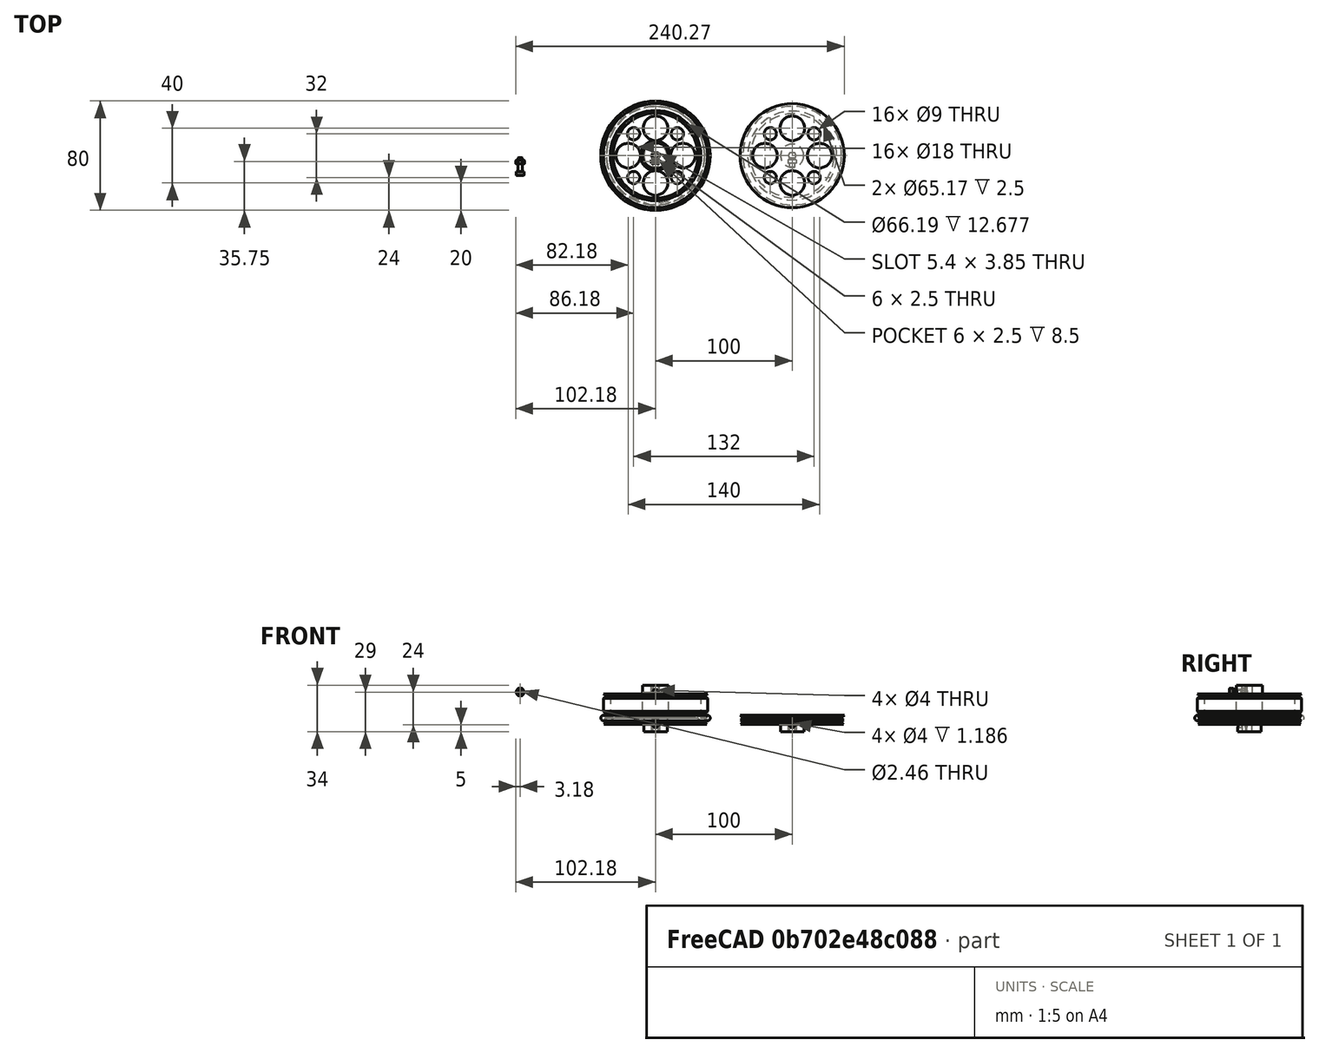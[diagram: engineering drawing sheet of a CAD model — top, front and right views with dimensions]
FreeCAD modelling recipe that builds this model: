
FCSTD DOCUMENT  (FreeCAD 0.19R24291 (Git))
Label: ruedas
License: All rights reserved
LicenseURL: http://en.wikipedia.org/wiki/All_rights_reserved
objects: Part::Cut×11, Part::Cylinder×10, Sketcher::SketchObject×8, PartDesign::Body×6, Part::Feature×6, Part::FeaturePython×6, Part::MultiFuse×5, App::Part×4, Part::Box×3, Part::Extrusion×3, Part::Revolution×2, PartDesign::Revolution×2, Mesh::Feature×2, PartDesign::FeatureBase×1, PartDesign::Pocket×1, PartDesign::PolarPattern×1, Part::Chamfer×1
note: 69 computed .brp shape members not serialized (recipe doc carries the construction recipe); baked Part::Feature solids carry a one-line shape summary decoded from their .brp

FEATURE [PartDesign::Body] Body
  Origin = -> Origin
FEATURE [Sketcher::SketchObject] Sketch
  FullyConstrained = true
  MapMode = 5
  Placement = pos=(0,0,0) rot=(1,0,0;1.5708rad)
  Support = -> [XZ_Plane]
  sketch-geometry (8):
    g0: LineSegment StartX=0 StartY=2 StartZ=0 EndX=31 EndY=2 EndZ=0
    g1: LineSegment StartX=31 StartY=2 StartZ=0 EndX=33 EndY=4 EndZ=0
    g2: LineSegment StartX=33 StartY=4 StartZ=0 EndX=38 EndY=4 EndZ=0
    g3: LineSegment StartX=38 StartY=0 StartZ=0 EndX=0 EndY=0 EndZ=0
    g4: LineSegment StartX=0 StartY=0 StartZ=0 EndX=0 EndY=2 EndZ=0
    g5: Circle CenterX=37.5 CenterY=2 CenterZ=0 NormalX=0 NormalY=0 NormalZ=1 AngleXU=0 Radius=1
    g6: LineSegment StartX=38 StartY=4 StartZ=0 EndX=36.1315 EndY=2 EndZ=0
    g7: LineSegment StartX=36.1315 StartY=2 StartZ=0 EndX=38 EndY=0 EndZ=0
  constraints (24):
    c: PointOnObject(g0,g-2)
    c: Horizontal(g0)
    c: Coincident(g0,g1)
    c: Coincident(g1,g2)
    c: Horizontal(g2)
    c: Horizontal(g3)
    c: Coincident(g3,g4)
    c: Coincident(g4,g0)
    c: Radius(g5) = 1
    c: DistanceX(g-1,g5) = 37.5
    c: Vertical(g4)
    c: DistanceY(g4,g4) = 2
    c: DistanceY(g3,g1) = 4
    c: PointOnObject(g3,g-1)
    c: DistanceY(g3,g5) = 2
    c: Angle(g1,g0) = 2.35619
    c: Coincident(g2,g6)
    c: Coincident(g6,g7)
    c: Coincident(g7,g3)
    c: DistanceY(g3,g6) = 2
    c: Tangent(g7,g5)
    c: Tangent(g6,g5)
    c: DistanceX(g2,g2) = 5
    c: DistanceX(g3,g3) = 38
FEATURE [Part::Box] Box  label="Cubo"
  AttacherType = Attacher::AttachEngine3D
  Height = 10
  Length = 6
  Placement = pos=(-3,3,2.5) rot=(0,0,1;0rad)
  Width = 2.5
FEATURE [Part::Cylinder] Cylinder002  label="Cilindro002"
  Angle = 360
  AttacherType = Attacher::AttachEngine3D
  Height = 10
  Placement = pos=(0,10.2,6) rot=(1,0,0;1.5708rad)
  Radius = 2
FEATURE [Part::Cylinder] Cylinder  label="Cilindro"
  Angle = 360
  AttacherType = Attacher::AttachEngine3D
  Height = 11
  Radius = 8.5
FEATURE [Part::Cut] Cut
  Base = -> Cylinder
  Tool = -> Box
FEATURE [Part::Cut] Cut002
  Base = -> Cut
  Placement = pos=(0,0,3) rot=(1,0,0;3.14159rad)
  Tool = -> Cylinder002
FEATURE [PartDesign::Body] Body001
  Origin = -> Origin001
  Placement = pos=(0,0,-13) rot=(0,0,1;1.5708rad)
FEATURE [Sketcher::SketchObject] Sketch001
  FullyConstrained = true
  MapMode = 5
  Support = -> [XY_Plane001]
  sketch-geometry (4):
    g0: ArcOfCircle CenterX=0 CenterY=0 CenterZ=0 NormalX=0 NormalY=0 NormalZ=1 AngleXU=0 Radius=2.7 StartAngle=3.91867 EndAngle=5.5061
    g1: LineSegment StartX=-1.925 StartY=-1.89324 StartZ=0 EndX=-1.925 EndY=1.89324 EndZ=0
    g2: LineSegment StartX=1.925 StartY=-1.89324 StartZ=0 EndX=1.925 EndY=1.89324 EndZ=0
    g3: ArcOfCircle CenterX=0 CenterY=0 CenterZ=0 NormalX=0 NormalY=0 NormalZ=1 AngleXU=0 Radius=2.7 StartAngle=0.777082 EndAngle=2.36451
  constraints (12):
    c: Coincident(g0,g-1)
    c: Radius(g0) = 2.7
    c: Vertical(g2)
    c: Vertical(g1)
    c: Coincident(g0,g1)
    c: Coincident(g3,g1)
    c: Equal(g0,g3)
    c: Coincident(g0,g2)
    c: Coincident(g3,g2)
    c: Coincident(g0,g3)
    c: DistanceX(g1,g2) = 3.85
    c: Equal(g1,g2)
FEATURE [Part::Revolution] Revolve001
  Angle = 360
  Axis = (0,0,1)
  Base = (0,0,0)
  FaceMakerClass = Part::FaceMakerBullseye
  Placement = pos=(0,0,1) rot=(0,1,0;3.14159rad)
  Solid = false
  Source = -> Sketch
  Symmetric = false
FEATURE [Part::Extrusion] Extrude
  Base = -> Sketch001
  Dir = (0,0,1)
  DirMode = 2
  FaceMakerClass = Part::FaceMakerBullseye
  LengthFwd = 10
  LengthRev = 0
  Placement = pos=(0,0,-9) rot=(0,0,1;1.5708rad)
  Solid = true
  Symmetric = false
FEATURE [Part::Cut] Cut003
  Base = -> Cut002
  Placement = pos=(0,0,-3) rot=(0,0,1;0rad)
  Tool = -> Extrude
FEATURE [Part::Feature] Revolve001_solid  label="Revolve001 (Solid)"
  shape: bbox 76 x 76 x 4 mm, 6 faces (baked)
FEATURE [Part::MultiFuse] Fusion
  Shapes = -> [Revolve001_solid,Cut003]
FEATURE [Part::Cylinder] Cylinder003  label="Cilindro003"
  Angle = 360
  AttacherType = Attacher::AttachEngine3D
  Height = 10
  Placement = pos=(20,0,-7) rot=(0,0,1;0rad)
  Radius = 9
FEATURE [Part::Cylinder] Cylinder004  label="Cilindro004"
  Angle = 360
  AttacherType = Attacher::AttachEngine3D
  Height = 10
  Placement = pos=(16,-16,-7) rot=(0,0,1;0rad)
  Radius = 4.5
FEATURE [Part::FeaturePython] Array  # Draft array (typed FeaturePython)
  Angle = 360
  ArrayType = 1
  Axis = (0,0,1)
  Base = -> Cylinder003
  Center = (0,0,0)
  Fuse = false
  IntervalAxis = (0,0,0)
  IntervalX = (1,0,0)
  IntervalY = (0,1,0)
  IntervalZ = (0,0,0)
  NumberPolar = 4
  NumberX = 2
  NumberY = 2
  NumberZ = 1
FEATURE [Part::FeaturePython] Array001  # Draft array (typed FeaturePython)
  Angle = 360
  ArrayType = 1
  Axis = (0,0,1)
  Base = -> Cylinder004
  Center = (0,0,0)
  Fuse = false
  IntervalAxis = (0,0,0)
  IntervalX = (1,0,0)
  IntervalY = (0,1,0)
  IntervalZ = (0,0,0)
  NumberPolar = 4
  NumberX = 2
  NumberY = 2
  NumberZ = 1
FEATURE [Part::MultiFuse] Fusion001
  Shapes = -> [Array,Array001]
FEATURE [Part::Cut] Cut004
  Base = -> Fusion
  Tool = -> Fusion001
FEATURE [Sketcher::SketchObject] Sketch002
  AttachmentOffset = pos=(0,-1,0) rot=(0,0,1;0rad)
  FullyConstrained = true
  MapMode = 5
  Placement = pos=(2e-16,-2e-16,-1) rot=(0.57735,0.57735,0.57735;2.0944rad)
  Support = -> [YZ_Plane004]
  sketch-geometry (1):
    g0: Circle CenterX=38 CenterY=0 CenterZ=0 NormalX=0 NormalY=0 NormalZ=1 AngleXU=0 Radius=2
  constraints (3):
    c: PointOnObject(g0,g-1)
    c: DistanceX(g-1,g0) = 38
    c: Radius(g0) = 2
FEATURE [PartDesign::Revolution] Revolution
  Angle = 360
  Axis = (-2e-16,3e-16,1)
  Base = (2e-16,-2e-16,-1)
  Placement = pos=(0,0,0) rot=(0.57735,0.57735,0.57735;2.0944rad)
  Profile = -> Sketch002
  ReferenceAxis = -> Sketch002 [V_Axis]
  Refine = true
  Reversed = true
FEATURE [PartDesign::Body] Body002
  Group = -> [Sketch002,Revolution]
  Origin = -> Origin004
  Tip = -> Revolution
FEATURE [Part::Feature] Part002001  label="junta-torica-copy"
  shape: bbox 86.59 x 86.59 x 4 mm, 1 faces (baked)
FEATURE [App::Part] Part002  label="junta-torica-src"
  Group = -> [Body002,Part002001]
  Origin = -> Origin003
FEATURE [Part::Cylinder] Cylinder005  label="Cilindro005"
  Angle = 360
  AttacherType = Attacher::AttachEngine3D
  Height = 10
  Placement = pos=(20,0,-7) rot=(0,0,1;0rad)
  Radius = 9
FEATURE [Sketcher::SketchObject] Sketch003
  FullyConstrained = true
  MapMode = 5
  Placement = pos=(0,0,0) rot=(1,0,0;1.5708rad)
  Support = -> [XZ_Plane007]
  sketch-geometry (12):
    g0: LineSegment StartX=0 StartY=2 StartZ=0 EndX=30.5858 EndY=2 EndZ=0
    g1: LineSegment StartX=30.5858 StartY=2 StartZ=0 EndX=32.5858 EndY=4 EndZ=0
    g2: LineSegment StartX=38.0858 StartY=0 StartZ=0 EndX=0 EndY=0 EndZ=0
    g3: LineSegment StartX=0 StartY=0 StartZ=0 EndX=0 EndY=2 EndZ=0
    g4: Circle CenterX=37.5 CenterY=2 CenterZ=0 NormalX=0 NormalY=0 NormalZ=1 AngleXU=0 Radius=1
    g5: LineSegment StartX=37.5858 StartY=3.5 StartZ=0 EndX=36.0858 EndY=2 EndZ=0
    g6: LineSegment StartX=36.0858 StartY=2 StartZ=0 EndX=38.0858 EndY=0 EndZ=0
    g7: LineSegment StartX=37.5858 StartY=3.5 StartZ=0 EndX=36.0858 EndY=4.99999 EndZ=0
    g8: LineSegment StartX=36.0858 StartY=4.99999 StartZ=0 EndX=37.5858 EndY=6.50001 EndZ=0
    g9: LineSegment StartX=37.5858 StartY=6.50001 StartZ=0 EndX=32.5858 EndY=6.50001 EndZ=0
    g10: LineSegment StartX=32.5858 StartY=6.50001 StartZ=0 EndX=32.5858 EndY=4 EndZ=0
    g11: Circle CenterX=37.5 CenterY=5 CenterZ=0 NormalX=0 NormalY=0 NormalZ=1 AngleXU=0 Radius=1
  constraints (36):
    c: PointOnObject(g0,g-2)
    c: Horizontal(g0)
    c: Coincident(g0,g1)
    c: Horizontal(g2)
    c: Coincident(g2,g3)
    c: Coincident(g3,g0)
    c: Radius(g4) = 1
    c: DistanceX(g-1,g4) = 37.5
    c: Vertical(g3)
    c: DistanceY(g3,g3) = 2
    c: DistanceY(g2,g1) = 4
    c: PointOnObject(g2,g-1)
    c: DistanceY(g2,g4) = 2
    c: Angle(g1,g0) = 2.35619
    c: Coincident(g5,g6)
    c: Coincident(g6,g2)
    c: DistanceY(g2,g5) = 2
    c: Tangent(g6,g4)
    c: Tangent(g5,g4)
    c: DistanceX(g1,g5) = 5
    c: Coincident(g7,g8)
    c: Horizontal(g9)
    c: Coincident(g9,g10)
    c: Vertical(g10)
    c: Coincident(g1,g10)
    c: Radius(g11) = 1
    c: DistanceX(g11,g4) = 0
    c: DistanceX(g5,g7) = 0
    c: Tangent(g8,g11)
    c: Tangent(g11,g7)
    c: Coincident(g8,g9)
    c: Coincident(g5,g7)
    c: DistanceX(g5,g8) = 0
    c: DistanceY(g4,g11) = 3
    c: Angle(g6,g5) = 1.5708
    c: Angle(g7,g8) = 1.5708
FEATURE [Part::Revolution] Revolve002
  Angle = 360
  Axis = (0,0,1)
  Base = (0,0,0)
  FaceMakerClass = Part::FaceMakerBullseye
  Placement = pos=(0,0,1) rot=(0,1,0;3.14159rad)
  Solid = false
  Source = -> Sketch003
  Symmetric = false
FEATURE [Part::Feature] Revolve001_solid001  label="Revolve001 (Solid)001"
  shape: bbox 76.17 x 76.17 x 6.5 mm, 9 faces (baked)
FEATURE [Part::Cylinder] Cylinder006  label="Cilindro006"
  Angle = 360
  AttacherType = Attacher::AttachEngine3D
  Height = 11
  Radius = 8.5
FEATURE [PartDesign::Body] Body004
  Origin = -> Origin007
  Placement = pos=(0,0,-13) rot=(0,0,1;1.5708rad)
FEATURE [Part::Cylinder] Cylinder007  label="Cilindro007"
  Angle = 360
  AttacherType = Attacher::AttachEngine3D
  Height = 10
  Placement = pos=(16,-16,-7) rot=(0,0,1;0rad)
  Radius = 4.5
FEATURE [Part::FeaturePython] Array002  # Draft array (typed FeaturePython)
  Angle = 360
  ArrayType = 1
  Axis = (0,0,1)
  Base = -> Cylinder007
  Center = (0,0,0)
  Fuse = false
  IntervalAxis = (0,0,0)
  IntervalX = (1,0,0)
  IntervalY = (0,1,0)
  IntervalZ = (0,0,0)
  NumberPolar = 4
  NumberX = 2
  NumberY = 2
  NumberZ = 1
FEATURE [Part::Box] Box001  label="Cubo001"
  AttacherType = Attacher::AttachEngine3D
  Height = 10
  Length = 6
  Placement = pos=(-3,3,2.5) rot=(0,0,1;0rad)
  Width = 2.5
FEATURE [Part::Cut] Cut005
  Base = -> Cylinder006
  Tool = -> Box001
FEATURE [Part::FeaturePython] Array003  # Draft array (typed FeaturePython)
  Angle = 360
  ArrayType = 1
  Axis = (0,0,1)
  Base = -> Cylinder005
  Center = (0,0,0)
  Fuse = false
  IntervalAxis = (0,0,0)
  IntervalX = (1,0,0)
  IntervalY = (0,1,0)
  IntervalZ = (0,0,0)
  NumberPolar = 4
  NumberX = 2
  NumberY = 2
  NumberZ = 1
FEATURE [Part::MultiFuse] Fusion003
  Shapes = -> [Array003,Array002]
FEATURE [Part::Cylinder] Cylinder008  label="Cilindro008"
  Angle = 360
  AttacherType = Attacher::AttachEngine3D
  Height = 10
  Placement = pos=(0,10.2,6) rot=(1,0,0;1.5708rad)
  Radius = 2
FEATURE [Part::Cut] Cut006
  Base = -> Cut005
  Placement = pos=(0,0,3) rot=(1,0,0;3.14159rad)
  Tool = -> Cylinder008
FEATURE [Sketcher::SketchObject] Sketch004
  FullyConstrained = true
  MapMode = 5
  Support = -> [XY_Plane006]
  sketch-geometry (4):
    g0: ArcOfCircle CenterX=0 CenterY=0 CenterZ=0 NormalX=0 NormalY=0 NormalZ=1 AngleXU=0 Radius=2.7 StartAngle=3.91867 EndAngle=5.5061
    g1: LineSegment StartX=-1.925 StartY=-1.89324 StartZ=0 EndX=-1.925 EndY=1.89324 EndZ=0
    g2: LineSegment StartX=1.925 StartY=-1.89324 StartZ=0 EndX=1.925 EndY=1.89324 EndZ=0
    g3: ArcOfCircle CenterX=0 CenterY=0 CenterZ=0 NormalX=0 NormalY=0 NormalZ=1 AngleXU=0 Radius=2.7 StartAngle=0.777082 EndAngle=2.36451
  constraints (12):
    c: Coincident(g0,g-1)
    c: Radius(g0) = 2.7
    c: Vertical(g2)
    c: Vertical(g1)
    c: Coincident(g0,g1)
    c: Coincident(g3,g1)
    c: Equal(g0,g3)
    c: Coincident(g0,g2)
    c: Coincident(g3,g2)
    c: Coincident(g0,g3)
    c: DistanceX(g1,g2) = 3.85
    c: Equal(g1,g2)
FEATURE [Part::Extrusion] Extrude001
  Base = -> Sketch004
  Dir = (0,0,1)
  DirMode = 2
  FaceMakerClass = Part::FaceMakerBullseye
  LengthFwd = 10
  LengthRev = 0
  Placement = pos=(0,0,-9) rot=(0,0,1;1.5708rad)
  Solid = true
  Symmetric = false
FEATURE [Part::Cut] Cut008
  Base = -> Cut006
  Placement = pos=(0,0,-3) rot=(0,0,1;0rad)
  Tool = -> Extrude001
FEATURE [Part::MultiFuse] Fusion002
  Shapes = -> [Cut008,Revolve001_solid001]
FEATURE [Part::Cut] Cut007
  Base = -> Fusion002
  Tool = -> Fusion003
FEATURE [PartDesign::FeatureBase] BaseFeature
  BaseFeature = -> Revolve002
FEATURE [PartDesign::Body] Body003
  BaseFeature = -> Revolve002
  Group = -> [BaseFeature]
  Origin = -> Origin006
  Tip = -> BaseFeature
FEATURE [PartDesign::Body] Body005  label="rueda-bruto"
  Origin = -> Origin009
FEATURE [Sketcher::SketchObject] Sketch005
  FullyConstrained = true
  MapMode = 5
  Placement = pos=(0,0,0) rot=(1,0,0;1.5708rad)
  Support = -> [XZ_Plane009]
  sketch-geometry (13):
    g0: LineSegment StartX=0 StartY=0 StartZ=0 EndX=38.0858 EndY=0 EndZ=0
    g1: LineSegment StartX=38.0858 StartY=0 StartZ=0 EndX=36.0858 EndY=2 EndZ=0
    g2: LineSegment StartX=36.0858 StartY=2 StartZ=0 EndX=38.09 EndY=4.00421 EndZ=0
    g3: LineSegment StartX=38.09 StartY=4.00421 StartZ=0 EndX=38.09 EndY=13.3268 EndZ=0
    g4: LineSegment StartX=38.09 StartY=13.3268 StartZ=0 EndX=35.8095 EndY=15 EndZ=0
    g5: LineSegment StartX=35.8095 StartY=15 StartZ=0 EndX=38.0948 EndY=16.6767 EndZ=0
    g6: LineSegment StartX=38.0948 StartY=16.6767 StartZ=0 EndX=33.0948 EndY=16.6767 EndZ=0
    g7: LineSegment StartX=33.0948 StartY=16.6767 StartZ=0 EndX=33.0948 EndY=4 EndZ=0
    g8: LineSegment StartX=33.0948 StartY=4 StartZ=0 EndX=31.0948 EndY=2 EndZ=0
    g9: LineSegment StartX=31.0948 StartY=2 StartZ=0 EndX=0 EndY=2 EndZ=0
    g10: LineSegment StartX=0 StartY=2 StartZ=0 EndX=0 EndY=0 EndZ=0
    g11: Circle CenterX=37.5 CenterY=2 CenterZ=0 NormalX=0 NormalY=0 NormalZ=1 AngleXU=0 Radius=1
    g12: Circle CenterX=37.5 CenterY=15 CenterZ=0 NormalX=0 NormalY=0 NormalZ=1 AngleXU=0 Radius=1
  constraints (38):
    c: Coincident(g-1,g0)
    c: Horizontal(g0)
    c: Coincident(g0,g1)
    c: Coincident(g1,g2)
    c: Coincident(g2,g3)
    c: Vertical(g3)
    c: Coincident(g3,g4)
    c: Coincident(g4,g5)
    c: Coincident(g5,g6)
    c: Horizontal(g6)
    c: Coincident(g6,g7)
    c: Vertical(g7)
    c: Coincident(g7,g8)
    c: Coincident(g8,g9)
    c: Horizontal(g9)
    c: Coincident(g9,g10)
    c: Coincident(g10,g0)
    c: PointOnObject(g9,g-2)
    c: DistanceY(g0,g9) = 2
    c: Parallel(g8,g2)
    c: Angle(g8,g9) = 2.35619
    c: DistanceY(g0,g7) = 4
    c: DistanceY(g0,g1) = 2
    c: DistanceX(g6,g6) = 5
    c: DistanceY(g1,g4) = 13
    c: Equal(g11,g12)
    c: Radius(g11) = 1
    c: DistanceX(g0,g11) = 37.5
    c: DistanceY(g0,g11) = 2
    c: Tangent(g1,g11)
    c: Tangent(g2,g11)
    c: DistanceX(g12,g11) = 0
    c: DistanceY(g11,g12) = 13
    c: Tangent(g4,g12)
    c: Tangent(g5,g12)
    c: DistanceX(g11,g2) = 0.59
    c: Equal(g1,g4)
    c: Equal(g5,g2)
FEATURE [PartDesign::Revolution] Revolution001
  Angle = 360
  Axis = (0,2e-16,1)
  Base = (0,0,0)
  Placement = pos=(0,0,0) rot=(1,0,0;1.5708rad)
  Profile = -> Sketch005
  ReferenceAxis = -> Sketch005 [V_Axis]
  Refine = true
  Reversed = true
FEATURE [Sketcher::SketchObject] Sketch006
  FullyConstrained = true
  MapMode = 5
  Placement = pos=(0,9e-16,2) rot=(0,0,1;3.14159rad)
  Support = -> [Revolution001]
  sketch-geometry (2):
    g0: Circle CenterX=0 CenterY=20 CenterZ=0 NormalX=0 NormalY=0 NormalZ=1 AngleXU=0 Radius=9
    g1: Circle CenterX=16 CenterY=16 CenterZ=0 NormalX=0 NormalY=0 NormalZ=1 AngleXU=0 Radius=4.5
  constraints (6):
    c: PointOnObject(g0,g-2)
    c: Radius(g0) = 9
    c: DistanceY(g-1,g0) = 20
    c: Radius(g1) = 4.5
    c: DistanceX(g-1,g1) = 16
    c: DistanceY(g-1,g1) = 16
FEATURE [PartDesign::Pocket] Pocket
  Length = 5
  Length2 = 100
  Placement = pos=(0,0,0) rot=(1,0,0;1.5708rad)
  Profile = -> Sketch006
  Refine = true
  Type = 0
FEATURE [PartDesign::PolarPattern] PolarPattern
  Angle = 360
  Axis = -> Sketch006 [N_Axis]
  BaseFeature = -> Pocket
  Occurrences = 4
  Originals = -> [Pocket]
  Placement = pos=(0,0,0) rot=(1,0,0;1.5708rad)
  Refine = true
FEATURE [Part::Box] Box002  label="Cubo002"
  AttacherType = Attacher::AttachEngine3D
  Height = 10
  Length = 6
  Placement = pos=(-3,3,12.5) rot=(0,0,1;0rad)
  Width = 2.5
FEATURE [Part::Cylinder] Cylinder009  label="Cilindro009"
  Angle = 360
  AttacherType = Attacher::AttachEngine3D
  Height = 10
  Placement = pos=(0,10.2,16) rot=(1,0,0;1.5708rad)
  Radius = 2
FEATURE [Part::Cylinder] Cylinder010  label="Cilindro010"
  Angle = 360
  AttacherType = Attacher::AttachEngine3D
  Height = 21
  Radius = 9.5
FEATURE [Part::Cut] Cut010
  Base = -> Cylinder010
  Tool = -> Box002
FEATURE [Part::Cut] Cut009
  Base = -> Cut010
  Placement = pos=(0,0,3) rot=(1,0,0;3.14159rad)
  Tool = -> Cylinder009
FEATURE [Sketcher::SketchObject] Sketch007
  FullyConstrained = true
  MapMode = 5
  Support = -> [XY_Plane010]
  sketch-geometry (4):
    g0: ArcOfCircle CenterX=0 CenterY=0 CenterZ=0 NormalX=0 NormalY=0 NormalZ=1 AngleXU=0 Radius=2.7 StartAngle=3.91867 EndAngle=5.5061
    g1: LineSegment StartX=-1.925 StartY=-1.89324 StartZ=0 EndX=-1.925 EndY=1.89324 EndZ=0
    g2: LineSegment StartX=1.925 StartY=-1.89324 StartZ=0 EndX=1.925 EndY=1.89324 EndZ=0
    g3: ArcOfCircle CenterX=0 CenterY=0 CenterZ=0 NormalX=0 NormalY=0 NormalZ=1 AngleXU=0 Radius=2.7 StartAngle=0.777082 EndAngle=2.36451
  constraints (12):
    c: Coincident(g0,g-1)
    c: Radius(g0) = 2.7
    c: Vertical(g2)
    c: Vertical(g1)
    c: Coincident(g0,g1)
    c: Coincident(g3,g1)
    c: Equal(g0,g3)
    c: Coincident(g0,g2)
    c: Coincident(g3,g2)
    c: Coincident(g0,g3)
    c: DistanceX(g1,g2) = 3.85
    c: Equal(g1,g2)
FEATURE [Part::Extrusion] Extrude002
  Base = -> Sketch007
  Dir = (0,0,1)
  DirMode = 2
  FaceMakerClass = Part::FaceMakerBullseye
  LengthFwd = 10
  LengthRev = 0
  Placement = pos=(0,0,-19) rot=(0,0,1;1.5708rad)
  Solid = true
  Symmetric = false
FEATURE [Part::Cut] Cut011
  Base = -> Cut009
  Placement = pos=(0,0,5) rot=(0,1,0;3.14159rad)
  Refine = true
  Tool = -> Extrude002
FEATURE [Part::MultiFuse] Fusion004
  Refine = true
  Shapes = -> [PolarPattern,Cut011]
FEATURE [Mesh::Feature] Mesh  label="Cut004 (Meshed)"
FEATURE [Mesh::Feature] Mesh001  label="Cut007 (Meshed)"
FEATURE [Part::Feature] Part002002002003  label="rueda-dos-juntas-copy"
  Placement = pos=(100,0,0) rot=(0,0,1;0rad)
  shape: bbox 76.17 x 76.17 x 12 mm, 32 faces (baked)
FEATURE [App::Part] Part002002  label="rueda-dos-juntas-src"
  Group = -> [Body003,Cut006,Cut005,Fusion003,Array003,Cylinder008,Sketch004,Cylinder005,Revolve001_solid001,Extrude001,Fusion002,Cylinder006,Cut008,Cylinder007,Array002,Box001,Cut007,Body004,Sketch003,Revolve002,Mesh001,Part002002002003]
  Origin = -> Origin005
  Placement = pos=(100,0,0) rot=(0,0,1;0rad)
FEATURE [Part::Feature] Cut004001  label="rueda-una-junta-copy"
  shape: bbox 76 x 76 x 12 mm, 29 faces (baked)
FEATURE [App::Part] Part  label="rueda-una-junta-src"
  Group = -> [Body,Body001,Sketch,Revolve001,Cylinder,Box,Cylinder002,Cut002,Sketch001,Cut,Extrude,Cut003,Revolve001_solid,Fusion,Cylinder003,Cylinder004,Array,Array001,Fusion001,Cut004,Mesh,Cut004001]
  Origin = -> Origin002
FEATURE [Part::Chamfer] Chamfer
  Base = -> Fusion004
  Edges = 1 edges r=1.5: [Edge31]
FEATURE [App::Part] Part002002002  label="rueda-dos-juntas-ancha-src"
  Group = -> [Body005,Cut009,Sketch007,Cut010,XY_Plane010,Box002,Cylinder010,Cylinder009,Extrude002,Cut011,Sketch005,Revolution001,Sketch006,PolarPattern,Pocket,Fusion004,Chamfer]
  Origin = -> Origin008
  Placement = pos=(-99,0,0) rot=(0,0,1;0rad)
FEATURE [Part::Feature] Chamfer001  label="rueda-dos-juntas-ancha-copy"
  shape: bbox 76.19 x 76.19 x 23 mm, 34 faces (baked)
FEATURE [Part::FeaturePython] Screw  label="M3x10-Screw"  # Fasteners workbench fastener (typed FeaturePython)
  Placement = pos=(-99,-11.5,18) rot=(1,0,0;1.5708rad)
  diameter = 3
  invert = false
  length = 3
  lengthCustom = 10
  matchOuter = false
  offset = 3
  thread = false
  type = 18
FEATURE [Part::FeaturePython] Nut  label="M3-Nut"  # Fasteners workbench fastener (typed FeaturePython)
  Placement = pos=(-99,-3.5,18) rot=(1,0,0;1.5708rad)
  baseObject = -> Screw [Edge14]
  diameter = 4
  invert = false
  matchOuter = false
  offset = 2
  thread = false
  type = 7
